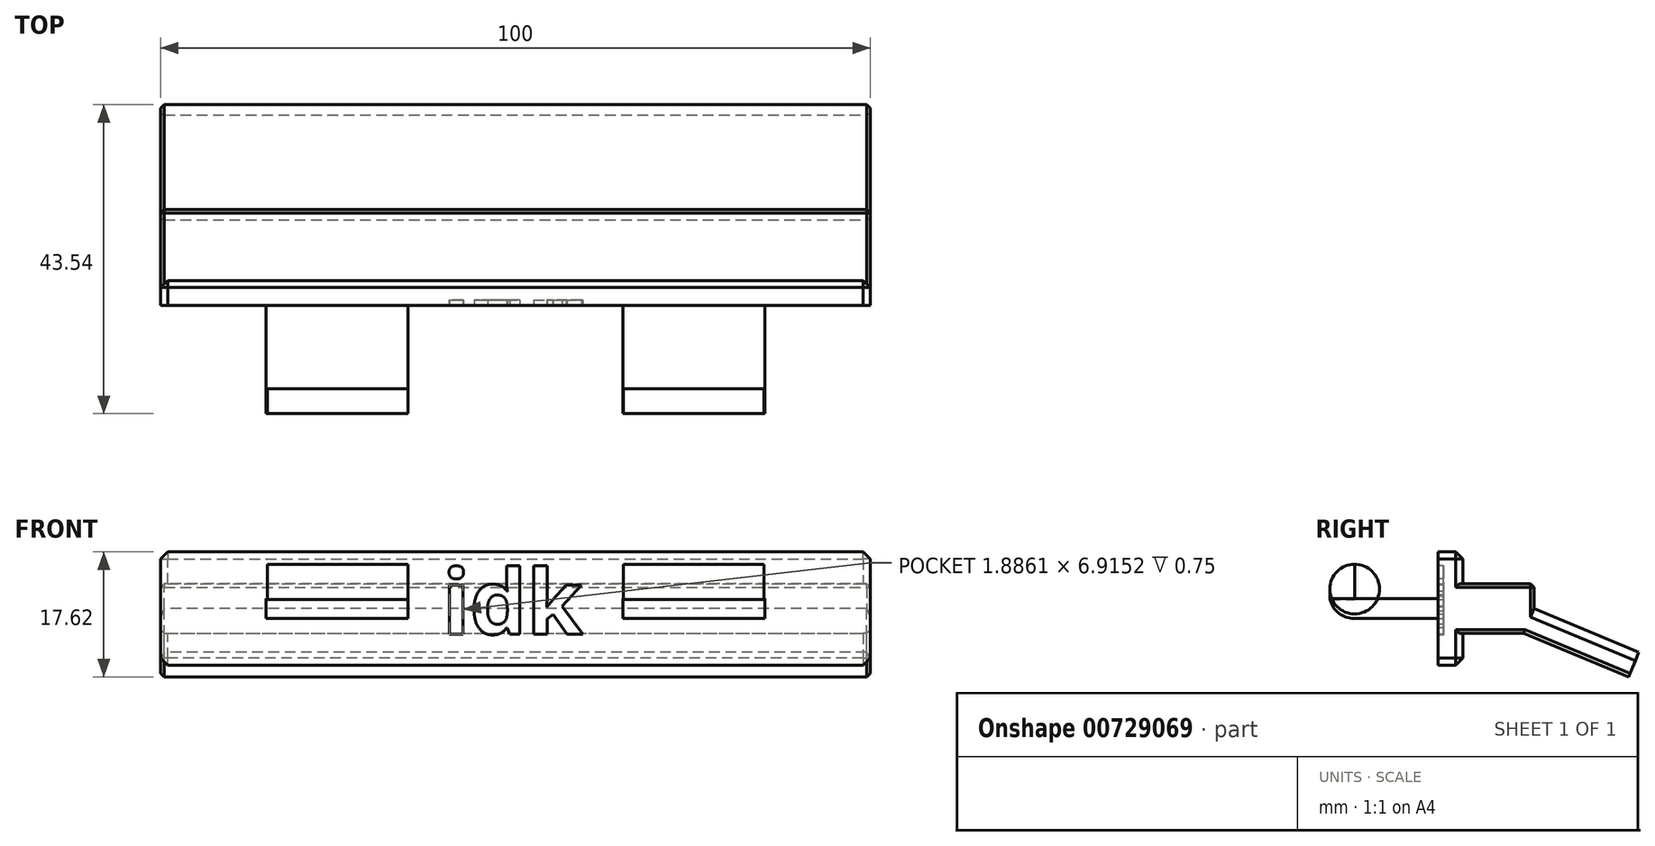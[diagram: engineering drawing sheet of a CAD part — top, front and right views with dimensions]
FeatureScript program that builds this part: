
annotation { "Feature Type Name" : "Feature", "Feature Type Description" : "" }
export const myFeature = defineFeature(function(context is Context, id is Id, definition is map)
    precondition{}
    {
        {
            var Q0;
            Q0=qCreatedBy(makeId("Front.planeOp"),FACE);
            var sketch = newSketch(context, id + "F0", { "sketchPlane" : qUnion([Q0])});
            skLineSegment(sketch, "E0.bottom", {"start": v(-50, 8) * mm, "end": v(50, 8) * mm});
            skLineSegment(sketch, "E0.top", {"start": v(-50, -8) * mm, "end": v(50, -8) * mm});
            skLineSegment(sketch, "E0.left", {"start": v(-50, 8) * mm, "end": v(-50, -8) * mm});
            skLineSegment(sketch, "E0.right", {"start": v(50, 8) * mm, "end": v(50, -8) * mm});
            skPoint(sketch, "E0.middle", {"position": v(0, 0) * mm});
            skSolve(sketch);
        }
        {
            var Q0;
            Q0=makeQuery(id+"F0.imprint","IMPRINT",FACE,{"disambiguationData":[TD([[makeQuery(id+"F0.imprint","IMPRINT",EDGE,{"derivedFrom":sQuery(id+"F0.wireOp",EDGE,"E0.bottom")}),-1.0]])]});
            extrude(context, id + "F1", {"entities" : qUnion([Q0]), "depth" : 3.5 * mm, "offsetDistance" : 25 * mm});
        }
        {
            var Q0;
            Q0=makeQuery(id+"F1.opExtrude","CAP_FACE",FACE,{"disambiguationData":[OSD([sQuery(id+"F0.wireOp",EDGE,"E0.bottom"),sQuery(id+"F0.wireOp",EDGE,"E0.top"),sQuery(id+"F0.wireOp",EDGE,"E0.left"),sQuery(id+"F0.wireOp",EDGE,"E0.right")])],"isStart":false});
            var sketch = newSketch(context, id + "F2", { "sketchPlane" : qUnion([Q0])});
            skLineSegment(sketch, "E1.bottom", {"start": v(-35.15, 1.4) * mm, "end": v(-15.15, 1.4) * mm});
            skLineSegment(sketch, "E1.top", {"start": v(-35.15, -1.4) * mm, "end": v(-15.15, -1.4) * mm});
            skLineSegment(sketch, "E1.left", {"start": v(-35.15, 1.4) * mm, "end": v(-35.15, -1.4) * mm});
            skLineSegment(sketch, "E1.right", {"start": v(-15.15, 1.4) * mm, "end": v(-15.15, -1.4) * mm});
            skPoint(sketch, "E1.middle", {"position": v(-25.15, 0) * mm});
            skLineSegment(sketch, "E2.bottom", {"start": v(15.15, 1.4) * mm, "end": v(35.15, 1.4) * mm});
            skLineSegment(sketch, "E2.top", {"start": v(15.15, -1.4) * mm, "end": v(35.15, -1.4) * mm});
            skLineSegment(sketch, "E2.left", {"start": v(15.15, 1.4) * mm, "end": v(15.15, -1.4) * mm});
            skLineSegment(sketch, "E2.right", {"start": v(35.15, 1.4) * mm, "end": v(35.15, -1.4) * mm});
            skPoint(sketch, "E2.middle", {"position": v(25.15, 0) * mm});
            skSolve(sketch);
        }
        {
            var Q0;
            Q0 = qSketchRegion(id + "F2", true);
            extrude(context, id + "F3", {"entities" : qUnion([Q0]), "operationType" : NewBodyOperationType.ADD, "depth" : 15.25 * mm, "offsetDistance" : 25 * mm});
        }
        {
            var Q0;
            Q0=qCreatedBy(makeId("Top.planeOp"),FACE);
            cPlane(context, id + "F4", {"entities" : qUnion([Q0]), "cplaneType" : CPlaneType.OFFSET, "offset" : 1.25 * mm, "width" : 150 * mm, "height" : 150 * mm});
        }
        {
            var Q0;
            Q0=qCreatedBy(id+"F4.planeOp",FACE);
            var sketch = newSketch(context, id + "F5", { "sketchPlane" : qUnion([Q0])});
            skLineSegment(sketch, "E3.bottom", {"start": v(-15.13, -18.76) * mm, "end": v(-34.93, -18.76) * mm});
            skLineSegment(sketch, "E3.top", {"start": v(-15.13, -15.26) * mm, "end": v(-34.93, -15.26) * mm});
            skLineSegment(sketch, "E3.left", {"start": v(-15.13, -18.76) * mm, "end": v(-15.13, -15.26) * mm});
            skLineSegment(sketch, "E3.right", {"start": v(-34.93, -18.76) * mm, "end": v(-34.93, -15.26) * mm});
            skSolve(sketch);
        }
        {
            var Q0;
            Q0 = qSketchRegion(id + "F5", true);
            extrude(context, id + "F6", {"entities" : qUnion([Q0]), "operationType" : NewBodyOperationType.ADD, "depth" : 5 * mm, "offsetDistance" : 25 * mm});
        }
        {
            var Q0;
            Q0=qCreatedBy(id+"F4.planeOp",FACE);
            var sketch = newSketch(context, id + "F7", { "sketchPlane" : qUnion([Q0])});
            skLineSegment(sketch, "E4.bottom", {"start": v(35.03, -18.76) * mm, "end": v(15.23, -18.76) * mm});
            skLineSegment(sketch, "E4.top", {"start": v(35.03, -15.26) * mm, "end": v(15.23, -15.26) * mm});
            skLineSegment(sketch, "E4.left", {"start": v(35.03, -18.76) * mm, "end": v(35.03, -15.26) * mm});
            skLineSegment(sketch, "E4.right", {"start": v(15.23, -18.76) * mm, "end": v(15.23, -15.26) * mm});
            skSolve(sketch);
        }
        {
            var Q0;
            Q0 = qSketchRegion(id + "F7", true);
            extrude(context, id + "F8", {"entities" : qUnion([Q0]), "operationType" : NewBodyOperationType.ADD, "depth" : 5 * mm, "offsetDistance" : 25 * mm});
        }
        {
            var Q0;
            Q0=makeQuery(id+"F1.opExtrude","CAP_FACE",FACE,{"disambiguationData":[OSD([sQuery(id+"F0.wireOp",EDGE,"E0.bottom"),sQuery(id+"F0.wireOp",EDGE,"E0.top"),sQuery(id+"F0.wireOp",EDGE,"E0.left"),sQuery(id+"F0.wireOp",EDGE,"E0.right")])],"isStart":true});
            var sketch = newSketch(context, id + "F9", { "sketchPlane" : qUnion([Q0])});
            skLineSegment(sketch, "E5.bottom", {"start": v(50, 3.5) * mm, "end": v(-50, 3.5) * mm});
            skLineSegment(sketch, "E5.top", {"start": v(50, -3.5) * mm, "end": v(-50, -3.5) * mm});
            skLineSegment(sketch, "E5.left", {"start": v(50, 3.5) * mm, "end": v(50, -3.5) * mm});
            skLineSegment(sketch, "E5.right", {"start": v(-50, 3.5) * mm, "end": v(-50, -3.5) * mm});
            skPoint(sketch, "E5.middle", {"position": v(0, 0) * mm});
            skSolve(sketch);
        }
        {
            var Q0;
            Q0=makeQuery(id+"F9.imprint","IMPRINT",FACE,{"disambiguationData":[TD([[makeQuery(id+"F9.imprint","IMPRINT",EDGE,{"derivedFrom":sQuery(id+"F9.wireOp",EDGE,"E5.bottom")}),1.0]])]});
            extrude(context, id + "F10", {"entities" : qUnion([Q0]), "operationType" : NewBodyOperationType.ADD, "depth" : 10 * mm, "offsetDistance" : 25 * mm});
        }
        {
            var Q0;
            Q0=makeQuery(id+"F3.opExtrude","CAP_EDGE",EDGE,{"disambiguationData":[OSD([sQuery(id+"F2.wireOp",EDGE,"E2.top")])],"isStart":false});
            var Q1;
            Q1=makeQuery(id+"F8.opExtrude","CAP_EDGE",EDGE,{"disambiguationData":[OSD([sQuery(id+"F7.wireOp",EDGE,"E4.bottom")])],"isStart":false});
            fillet(context, id + "F11", {"entities" : qUnion([Q0, Q1]), "radius" : 3.5 * mm, "tangentPropagation" : true, "allowEdgeOverflow" : false});
        }
        {
            var Q0;
            Q0=makeQuery(id+"F3.opExtrude","CAP_EDGE",EDGE,{"disambiguationData":[OSD([sQuery(id+"F2.wireOp",EDGE,"E1.top")])],"isStart":false});
            var Q1;
            Q1=makeQuery(id+"F6.opExtrude","CAP_EDGE",EDGE,{"disambiguationData":[OSD([sQuery(id+"F5.wireOp",EDGE,"E3.bottom")])],"isStart":false});
            fillet(context, id + "F12", {"entities" : qUnion([Q0, Q1]), "radius" : 3.5 * mm, "tangentPropagation" : true, "allowEdgeOverflow" : false});
        }
        {
            var Q0;
            Q0=makeQuery(id+"F1.opExtrude","CAP_EDGE",EDGE,{"disambiguationData":[OSD([sQuery(id+"F0.wireOp",EDGE,"E0.bottom")])],"isStart":true});
            var Q1;
            {var subQ0=sQuery(id+"F0.wireOp",EDGE,"E0.left");var subQ1=sQuery(id+"F0.wireOp",EDGE,"E0.bottom");Q1=makeQuery(id+"F10.boolean.opBoolean","SPLIT",EDGE,{"disambiguationData":[TD([makeQuery(id+"F1.opExtrude","SWEPT_FACE",FACE,{"disambiguationData":[OSD([subQ1])]})])],"derivedFrom":makeQuery(id+"F1.opExtrude","CAP_EDGE",EDGE,{"disambiguationData":[OSD([subQ0])],"isStart":true})});}
            var Q2;
            Q2=makeQuery(id+"F1.opExtrude","SWEPT_EDGE",EDGE,{"disambiguationData":[OSD([sQuery(id+"F0.wireOp",EDGE,"E0.bottom"),sQuery(id+"F0.wireOp",EDGE,"E0.left")])]});
            var Q3;
            {var subQ0=sQuery(id+"F0.wireOp",EDGE,"E0.left");var subQ1=sQuery(id+"F0.wireOp",EDGE,"E0.top");Q3=makeQuery(id+"F10.boolean.opBoolean","SPLIT",EDGE,{"disambiguationData":[TD([makeQuery(id+"F1.opExtrude","SWEPT_FACE",FACE,{"disambiguationData":[OSD([subQ1])]})])],"derivedFrom":makeQuery(id+"F1.opExtrude","CAP_EDGE",EDGE,{"disambiguationData":[OSD([subQ0])],"isStart":true})});}
            var Q4;
            Q4=makeQuery(id+"F1.opExtrude","SWEPT_EDGE",EDGE,{"disambiguationData":[OSD([sQuery(id+"F0.wireOp",EDGE,"E0.top"),sQuery(id+"F0.wireOp",EDGE,"E0.left")])]});
            var Q5;
            Q5=makeQuery(id+"F1.opExtrude","CAP_EDGE",EDGE,{"disambiguationData":[OSD([sQuery(id+"F0.wireOp",EDGE,"E0.top")])],"isStart":true});
            var Q6;
            Q6=makeQuery(id+"F1.opExtrude","SWEPT_EDGE",EDGE,{"disambiguationData":[OSD([sQuery(id+"F0.wireOp",EDGE,"E0.bottom"),sQuery(id+"F0.wireOp",EDGE,"E0.right")])]});
            var Q7;
            {var subQ0=sQuery(id+"F0.wireOp",EDGE,"E0.right");var subQ1=sQuery(id+"F0.wireOp",EDGE,"E0.bottom");Q7=makeQuery(id+"F10.boolean.opBoolean","SPLIT",EDGE,{"disambiguationData":[TD([makeQuery(id+"F1.opExtrude","SWEPT_FACE",FACE,{"disambiguationData":[OSD([subQ1])]})])],"derivedFrom":makeQuery(id+"F1.opExtrude","CAP_EDGE",EDGE,{"disambiguationData":[OSD([subQ0])],"isStart":true})});}
            var Q8;
            {var subQ0=sQuery(id+"F0.wireOp",EDGE,"E0.right");var subQ1=sQuery(id+"F0.wireOp",EDGE,"E0.top");Q8=makeQuery(id+"F10.boolean.opBoolean","SPLIT",EDGE,{"disambiguationData":[TD([makeQuery(id+"F1.opExtrude","SWEPT_FACE",FACE,{"disambiguationData":[OSD([subQ1])]})])],"derivedFrom":makeQuery(id+"F1.opExtrude","CAP_EDGE",EDGE,{"disambiguationData":[OSD([subQ0])],"isStart":true})});}
            var Q9;
            Q9=makeQuery(id+"F1.opExtrude","SWEPT_EDGE",EDGE,{"disambiguationData":[OSD([sQuery(id+"F0.wireOp",EDGE,"E0.top"),sQuery(id+"F0.wireOp",EDGE,"E0.right")])]});
            chamfer(context, id + "F13", {"entities" : qUnion([Q0, Q1, Q2, Q3, Q4, Q5, Q6, Q7, Q8, Q9]), "width" : 1 * mm, "tangentPropagation" : true});
        }
        {
            var Q0;
            Q0=makeQuery(id+"F10.opExtrude","SWEPT_EDGE",EDGE,{"disambiguationData":[OSD([sQuery(id+"F0.wireOp",EDGE,"E0.right"),sQuery(id+"F9.wireOp",EDGE,"E5.top"),sQuery(id+"F9.wireOp",EDGE,"E5.right")])]});
            var Q1;
            Q1=makeQuery(id+"F10.opExtrude","SWEPT_EDGE",EDGE,{"disambiguationData":[OSD([sQuery(id+"F0.wireOp",EDGE,"E0.right"),sQuery(id+"F9.wireOp",EDGE,"E5.bottom"),sQuery(id+"F9.wireOp",EDGE,"E5.right")])]});
            var Q2;
            Q2=makeQuery(id+"F10.opExtrude","CAP_FACE",FACE,{"disambiguationData":[OSD([sQuery(id+"F9.wireOp",EDGE,"E5.bottom"),sQuery(id+"F9.wireOp",EDGE,"E5.top"),sQuery(id+"F9.wireOp",EDGE,"E5.left"),sQuery(id+"F9.wireOp",EDGE,"E5.right")])],"isStart":false});
            var Q3;
            Q3=makeQuery(id+"F10.opExtrude","SWEPT_EDGE",EDGE,{"disambiguationData":[OSD([sQuery(id+"F0.wireOp",EDGE,"E0.left"),sQuery(id+"F9.wireOp",EDGE,"E5.bottom"),sQuery(id+"F9.wireOp",EDGE,"E5.left")])]});
            var Q4;
            Q4=makeQuery(id+"F10.opExtrude","SWEPT_EDGE",EDGE,{"disambiguationData":[OSD([sQuery(id+"F0.wireOp",EDGE,"E0.left"),sQuery(id+"F9.wireOp",EDGE,"E5.top"),sQuery(id+"F9.wireOp",EDGE,"E5.left")])]});
            chamfer(context, id + "F14", {"entities" : qUnion([Q0, Q1, Q2, Q3, Q4]), "width" : .5 * mm, "tangentPropagation" : true});
        }
        {
            var Q0;
            Q0=makeQuery(id+"F1.opExtrude","CAP_FACE",FACE,{"disambiguationData":[OSD([sQuery(id+"F0.wireOp",EDGE,"E0.bottom"),sQuery(id+"F0.wireOp",EDGE,"E0.top"),sQuery(id+"F0.wireOp",EDGE,"E0.left"),sQuery(id+"F0.wireOp",EDGE,"E0.right")])],"isStart":false});
            var sketch = newSketch(context, id + "F15", { "sketchPlane" : qUnion([Q0])});
            skText(sketch, "E6", { "text": "idk", "fontName": "OpenSans-Bold.ttf"});
            const initialGuessF15  = {"E6": [-0.01027, -0.00359, 1, 0, 0.00912]};
            skSetInitialGuess(sketch, initialGuessF15);
            skSolve(sketch);
        }
        {
            var Q0;
            Q0 = qSketchRegion(id + "F15", true);
            extrude(context, id + "F16", {"entities" : qUnion([Q0]), "operationType" : NewBodyOperationType.REMOVE, "oppositeDirection" : true, "depth" : .75 * mm, "offsetDistance" : 25 * mm});
        }
        {
            var Q0;
            {var subQ0=sQuery(id+"F9.wireOp",EDGE,"E5.top");Q0=makeQuery(id+"F14.opChamfer","BLEND_EDGE",EDGE,{"blendedFrom":[makeQuery(id+"F10.opExtrude","CAP_EDGE",EDGE,{"disambiguationData":[OSD([subQ0])],"isStart":false}),makeQuery(id+"F10.opExtrude","CAP_FACE",FACE,{"disambiguationData":[OSD([sQuery(id+"F9.wireOp",EDGE,"E5.bottom"),subQ0,sQuery(id+"F9.wireOp",EDGE,"E5.left"),sQuery(id+"F9.wireOp",EDGE,"E5.right")])],"isStart":false})],"blendedInto":[makeQuery(id+"F10.opExtrude","CAP_FACE",FACE,{"disambiguationData":[OSD([sQuery(id+"F9.wireOp",EDGE,"E5.bottom"),subQ0,sQuery(id+"F9.wireOp",EDGE,"E5.left"),sQuery(id+"F9.wireOp",EDGE,"E5.right")])],"isStart":false})]});}
            chamfer(context, id + "F17", {"entities" : qUnion([Q0]), "width" : 7.2 * mm, "tangentPropagation" : true});
        }
        {
            var Q0;
            Q0=makeQuery(id+"F17.opChamfer","BLEND_FACE",FACE,{"disambiguationData":[OSD([sQuery(id+"F9.wireOp",EDGE,"E5.bottom"),sQuery(id+"F9.wireOp",EDGE,"E5.top"),sQuery(id+"F9.wireOp",EDGE,"E5.left"),sQuery(id+"F9.wireOp",EDGE,"E5.right")])]});
            extrude(context, id + "F18", {"entities" : qUnion([Q0]), "operationType" : NewBodyOperationType.ADD, "depth" : 16 * mm, "offsetDistance" : 25 * mm});
        }
    });
